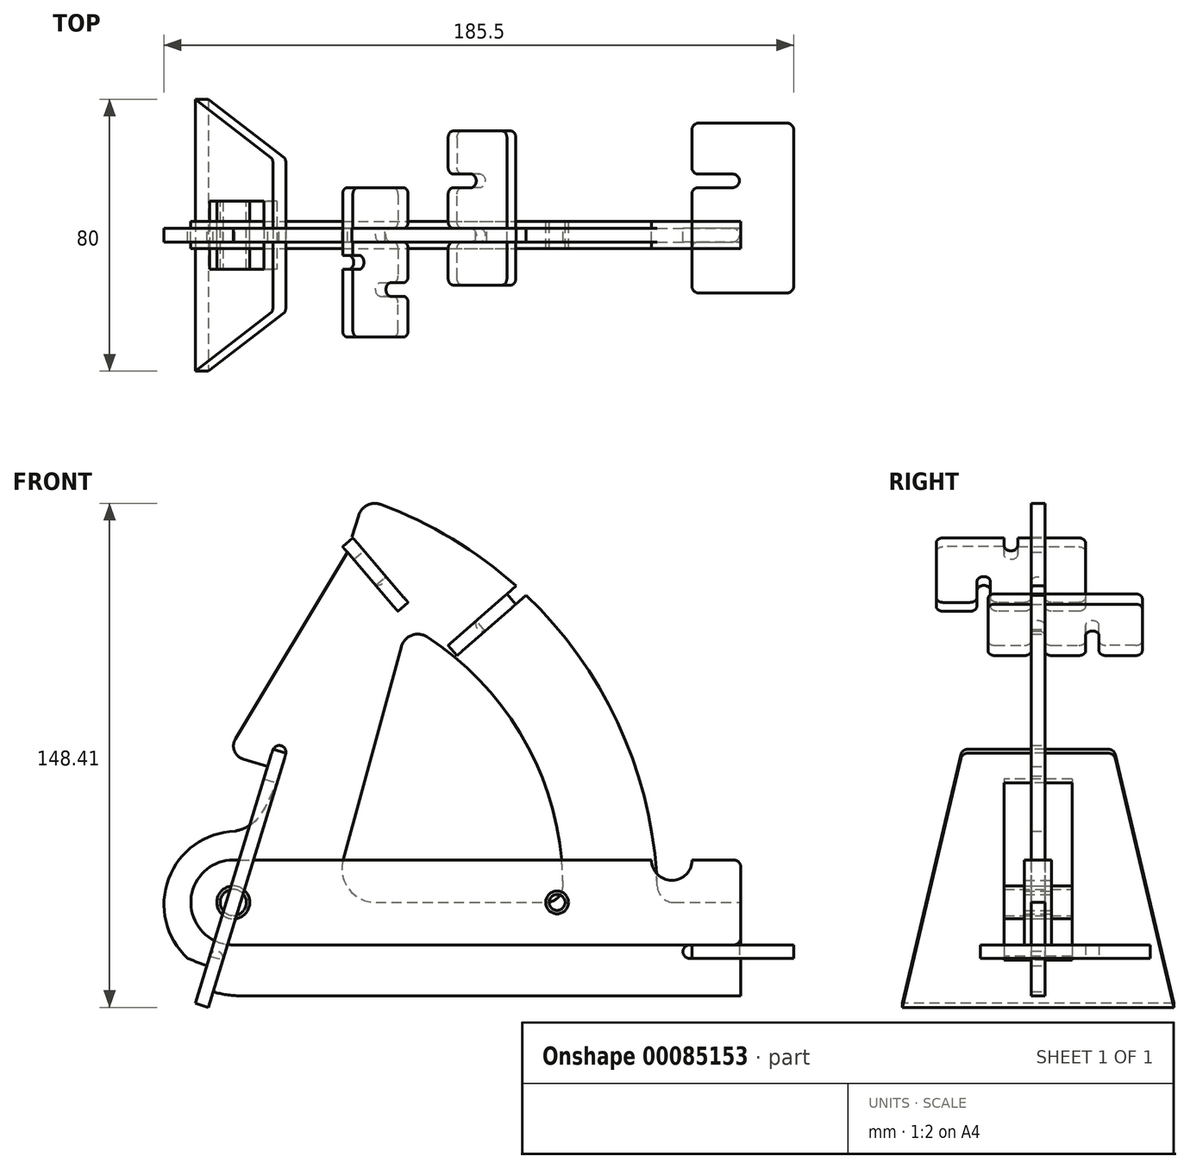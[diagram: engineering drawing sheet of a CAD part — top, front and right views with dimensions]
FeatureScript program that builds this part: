
annotation { "Feature Type Name" : "Feature", "Feature Type Description" : "" }
export const myFeature = defineFeature(function(context is Context, id is Id, definition is map)
    precondition{}
    {
        {
            var Q0;
            Q0=qCreatedBy(makeId("Front.planeOp"),FACE);
            var sketch = newSketch(context, id + "F0", { "sketchPlane" : qUnion([Q0])});
            skLineSegment(sketch, "E0", {"start": v(39.9, 0) * mm, "end": v(90.03, 0) * mm});
            skLineSegment(sketch, "E1.trimOffspring", {"start": v(31.52, 103.11) * mm, "end": v(34.85, 113.98) * mm});
            skLineSegment(sketch, "E2", {"start": v(0, -27.5) * mm, "end": v(147.4, -27.5) * mm});
            skPoint(sketch, "E3", {"position": v(95.8, 102.09) * mm});
            skArc(sketch, "E4", {"start": v(-27.2, -4.05) * mm, "mid": v(-27.13, -4.48) * mm, "end": v(-27.06, -4.91) * mm});
            skLineSegment(sketch, "E5", {"start": v(205.4, -14.5) * mm, "end": v(168.54, -14.5) * mm, "construction": true});
            skLineSegment(sketch, "E6", {"start": v(147.4, -14.5) * mm, "end": v(132.4, -14.5) * mm});
            skArc(sketch, "E7.0.endCap", {"start": v(132.4, -16.5) * mm, "mid": v(130.4, -14.5) * mm, "end": v(132.4, -12.5) * mm});
            skLineSegment(sketch, "E7.0.left", {"start": v(147.4, -16.5) * mm, "end": v(132.4, -16.5) * mm});
            skLineSegment(sketch, "E7.0.right", {"start": v(147.4, -12.5) * mm, "end": v(132.4, -12.5) * mm});
            skLineSegment(sketch, "E8", {"start": v(71.33, 81.91) * mm, "end": v(102.2, 108.89) * mm});
            skArc(sketch, "E9.0.startCap", {"start": v(72.62, 80.38) * mm, "mid": v(69.81, 80.6) * mm, "end": v(70.01, 83.42) * mm});
            skArc(sketch, "E9.0.endCap", {"start": v(100.87, 110.4) * mm, "mid": v(103.7, 110.2) * mm, "end": v(103.5, 107.38) * mm});
            skLineSegment(sketch, "E9.0.left", {"start": v(70.01, 83.42) * mm, "end": v(100.87, 110.4) * mm});
            skLineSegment(sketch, "E9.0.right", {"start": v(85.33, 91.49) * mm, "end": v(103.5, 107.38) * mm});
            skLineSegment(sketch, "E10", {"start": v(-8.04, -26.3) * mm, "end": v(-8.04, -26.3) * mm});
            skLineSegment(sketch, "E11", {"start": v(47.42, 75.33) * mm, "end": v(30.26, 12.64) * mm});
            skArc(sketch, "E12.filletArc", {"start": v(30.26, 12.64) * mm, "mid": v(31.95, 3.93) * mm, "end": v(39.9, 0) * mm});
            skPoint(sketch, "E13.visualSharp", {"position": v(52.17, 92.67) * mm});
            skPoint(sketch, "E14.endSnap0", {"position": v(-12.5, 0) * mm});
            skLineSegment(sketch, "E15", {"start": v(22.8, 74.55) * mm, "end": v(7.16, 23.42) * mm});
            skLineSegment(sketch, "E16", {"start": v(17.75, 71.72) * mm, "end": v(-20.77, -54.27) * mm, "construction": true});
            skPoint(sketch, "E17.startSnap0", {"position": v(11.4, 37.28) * mm});
            skLineSegment(sketch, "E18", {"start": v(4.72, 22.28) * mm, "end": v(-9.93, -25.64) * mm, "construction": true});
            skLineSegment(sketch, "E19", {"start": v(-7.1, -16.37) * mm, "end": v(-12.67, -34.6) * mm});
            skArc(sketch, "E20.0.startCap", {"start": v(-9, -15.78) * mm, "mid": v(-6.51, -14.46) * mm, "end": v(-5.18, -16.95) * mm});
            skLineSegment(sketch, "E20.0.left", {"start": v(-5.18, -16.95) * mm, "end": v(-10.77, -35.22) * mm});
            skLineSegment(sketch, "E20.0.right", {"start": v(-9, -15.78) * mm, "end": v(-14.6, -34.05) * mm});
            skPoint(sketch, "E21.visualSharp", {"position": v(-27.5, 0) * mm});
            skArc(sketch, "E22", {"start": v(95.03, 5.02) * mm, "mid": v(84.27, 46.7) * mm, "end": v(54.95, 78.21) * mm});
            skLineSegment(sketch, "E23", {"start": v(-60.53, 0) * mm, "end": v(147.4, 0) * mm, "construction": true});
            skCircle(sketch, "E24", {"center": v(-2.1, 0) * mm, "radius": 4.85 * mm});
            skArc(sketch, "E25", {"start": v(-2.1, 12.5) * mm, "mid": v(-14.6, 0) * mm, "end": v(-2.1, -12.5) * mm});
            skLineSegment(sketch, "E26", {"start": v(86.7, 92.43) * mm, "end": v(-27.06, -4.91) * mm, "construction": true});
            skLineSegment(sketch, "E27", {"start": v(147.4, 0) * mm, "end": v(147.4, -27.5) * mm});
            skPoint(sketch, "E28.visualSharp", {"position": v(124.1, 0) * mm});
            skPoint(sketch, "E29.visualSharp", {"position": v(49.15, 81.65) * mm});
            skArc(sketch, "E29.filletArc", {"start": v(54.95, 78.21) * mm, "mid": v(50.46, 78.68) * mm, "end": v(47.42, 75.33) * mm});
            skPoint(sketch, "E30.visualSharp", {"position": v(94.9, 0) * mm});
            skArc(sketch, "E30.filletArc", {"start": v(90.03, 0) * mm, "mid": v(93.57, 1.47) * mm, "end": v(95.03, 5.02) * mm});
            skLineSegment(sketch, "E31", {"start": v(32.22, 105.38) * mm, "end": v(61.64, 70.99) * mm, "construction": true});
            skLineSegment(sketch, "E32", {"start": v(32.22, 105.38) * mm, "end": v(24.37, 114.54) * mm, "construction": true});
            skLineSegment(sketch, "E33", {"start": v(40.67, 95.5) * mm, "end": v(30.35, 107.56) * mm});
            skArc(sketch, "E34.0.startCap", {"start": v(42.19, 96.8) * mm, "mid": v(41.97, 93.98) * mm, "end": v(39.15, 94.2) * mm});
            skArc(sketch, "E34.0.endCap", {"start": v(28.83, 106.26) * mm, "mid": v(29.05, 109.08) * mm, "end": v(31.87, 108.86) * mm});
            skLineSegment(sketch, "E34.0.left", {"start": v(39.15, 94.2) * mm, "end": v(28.83, 106.26) * mm});
            skLineSegment(sketch, "E34.0.right", {"start": v(42.19, 96.8) * mm, "end": v(31.87, 108.86) * mm});
            skPoint(sketch, "E35.orphan", {"position": v(49.12, 85.62) * mm});
            skArc(sketch, "E36", {"start": v(-9.88, -18.62) * mm, "mid": v(-12.73, -17.58) * mm, "end": v(-15.53, -16.42) * mm});
            skArc(sketch, "E37.trimOffspring", {"start": v(-8.04, -26.3) * mm, "mid": v(-4.06, -27.2) * mm, "end": v(0, -27.5) * mm});
            skLineSegment(sketch, "E38", {"start": v(-2.1, 12.5) * mm, "end": v(147.4, 12.5) * mm});
            skLineSegment(sketch, "E39", {"start": v(-2.1, -12.5) * mm, "end": v(147.4, -12.5) * mm});
            skArc(sketch, "E40", {"start": v(61.64, 70.99) * mm, "mid": v(85.04, 38.87) * mm, "end": v(93.31, 0) * mm, "construction": true});
            skCircle(sketch, "E41", {"center": v(93.31, 0) * mm, "radius": 3.35 * mm});
            skLineSegment(sketch, "E42", {"start": v(147.4, -12.5) * mm, "end": v(147.4, 12.5) * mm});
            skCircle(sketch, "E43", {"center": v(127.1, 12.5) * mm, "radius": 6 * mm});
            skArc(sketch, "E44", {"start": v(122.82, 4.8) * mm, "mid": v(99.13, 73.35) * mm, "end": v(41.37, 117.2) * mm});
            skLineSegment(sketch, "E45", {"start": v(122.9, 0) * mm, "end": v(122.9, -27.5) * mm, "construction": true});
            skPoint(sketch, "E46.visualSharp", {"position": v(36.36, 118.94) * mm});
            skArc(sketch, "E46.filletArc", {"start": v(41.37, 117.2) * mm, "mid": v(37.41, 117) * mm, "end": v(34.85, 113.98) * mm});
            skLineSegment(sketch, "E47", {"start": v(70.01, 83.42) * mm, "end": v(72.62, 80.38) * mm, "construction": true});
            skLineSegment(sketch, "E48", {"start": v(127.81, 0) * mm, "end": v(147.4, 0) * mm});
            skPoint(sketch, "E49.visualSharp", {"position": v(122.9, 0) * mm});
            skArc(sketch, "E49.filletArc", {"start": v(122.82, 4.8) * mm, "mid": v(124.35, 1.4) * mm, "end": v(127.81, 0) * mm});
            skLineSegment(sketch, "E50", {"start": v(72.62, 80.38) * mm, "end": v(85.33, 91.49) * mm});
            skLineSegment(sketch, "E51", {"start": v(11.43, 44.22) * mm, "end": v(9.97, 39.44) * mm});
            skArc(sketch, "E52.0.startCap", {"start": v(9.52, 44.8) * mm, "mid": v(12.01, 46.14) * mm, "end": v(13.34, 43.64) * mm});
            skLineSegment(sketch, "E52.0.left", {"start": v(13.34, 43.64) * mm, "end": v(11.88, 38.86) * mm});
            skLineSegment(sketch, "E52.0.right", {"start": v(9.52, 44.8) * mm, "end": v(8.05, 40.03) * mm});
            skLineSegment(sketch, "E53", {"start": v(0, -27.5) * mm, "end": v(-37.92, -27.5) * mm, "construction": true});
            skPoint(sketch, "E54", {"position": v(-10.5, -27.5) * mm});
            skLineSegment(sketch, "E55", {"start": v(8.05, 40.03) * mm, "end": v(0.8, 42.25) * mm});
            skPoint(sketch, "E56.visualSharp", {"position": v(-5.3, 44.1) * mm});
            skArc(sketch, "E56.filletArc", {"start": v(-1.47, 48.13) * mm, "mid": v(-1.77, 44.64) * mm, "end": v(0.8, 42.25) * mm});
            skLineSegment(sketch, "E57", {"start": v(-1.47, 48.13) * mm, "end": v(31.52, 103.11) * mm});
            skFitSpline(sketch, "E58", {"points": [v(11.4, 37.28) * mm, v(4.32, 23.93) * mm, v(-1.58, 20.95) * mm], "startDerivative": vector(-10.84, -26.6) * mm, "endDerivative": vector(-15.43, -4.6) * mm});
            skArc(sketch, "E59.trimOffspring", {"start": v(-1.58, 20.95) * mm, "mid": v(-21.15, 6.97) * mm, "end": v(-15.53, -16.42) * mm});
            skCircle(sketch, "E60", {"center": v(-2.1, 0) * mm, "radius": 3.85 * mm});
            skCircle(sketch, "E61", {"center": v(93.31, 0) * mm, "radius": 2.35 * mm});
            skSolve(sketch);
        }
        {
            var Q0;
            {var subQ0=sQuery(id+"F0.wireOp",EDGE,"bf617d19-ef6b-4165-97db-2c77cec7c9c5");var subQ1=sQuery(id+"F0.wireOp",EDGE,"E0");var subQ2=makeQuery(id+"F0.imprint","INTERSECT",VERTEX,{"disambiguationData":[OD(0.0)],"derivedFrom":[subQ1,subQ0]});Q0=makeQuery(id+"F0.imprint","IMPRINT",FACE,{"disambiguationData":[TD([[makeQuery(id+"F0.imprint","IMPRINT",EDGE,{"disambiguationData":[TD([[subQ2,-1.0]])],"derivedFrom":subQ1}),-1.0]])]});}
            var Q1;
            {var subQ13=sQuery(id+"F0.wireOp",EDGE,"634d09b6-26d1-4d0d-8a2f-190011938a09");Q1=makeQuery(id+"F0.imprint","IMPRINT",FACE,{"disambiguationData":[TD([[makeQuery(id+"F0.imprint","IMPRINT",EDGE,{"derivedFrom":subQ13}),-1.0]])]});}
            var Q2;
            {var subQ11=sQuery(id+"F0.wireOp",EDGE,"634d09b6-26d1-4d0d-8a2f-190011938a09");Q2=makeQuery(id+"F0.imprint","IMPRINT",FACE,{"disambiguationData":[TD([[makeQuery(id+"F0.imprint","IMPRINT",EDGE,{"derivedFrom":subQ11}),1.0]])]});}
            var Q3;
            {var subQ1=sQuery(id+"F0.wireOp",EDGE,"f24d4ff7-ed1b-4c84-8cf0-a38a7c947f8a.converted");var subQ3=sQuery(id+"F0.wireOp",EDGE,"88331fb1-bad4-4c96-8eaa-def0ac8052ee");var subQ4=makeQuery(id+"F0.imprint","INTERSECT",VERTEX,{"disambiguationData":[OD(0.0)],"derivedFrom":[subQ1,subQ3]});Q3=makeQuery(id+"F0.imprint","IMPRINT",FACE,{"disambiguationData":[TD([[makeQuery(id+"F0.imprint","IMPRINT",EDGE,{"disambiguationData":[TD([[subQ4,-1.0]])],"derivedFrom":subQ3}),1.0]])]});}
            var Q4;
            {var subQ1=sQuery(id+"F0.wireOp",EDGE,"f24d4ff7-ed1b-4c84-8cf0-a38a7c947f8a.converted");var subQ3=sQuery(id+"F0.wireOp",EDGE,"88331fb1-bad4-4c96-8eaa-def0ac8052ee");var subQ4=makeQuery(id+"F0.imprint","INTERSECT",VERTEX,{"disambiguationData":[OD(1.0)],"derivedFrom":[subQ1,subQ3]});Q4=makeQuery(id+"F0.imprint","IMPRINT",FACE,{"disambiguationData":[TD([[makeQuery(id+"F0.imprint","IMPRINT",EDGE,{"disambiguationData":[TD([[subQ4,1.0]])],"derivedFrom":subQ3}),1.0]])]});}
            var Q5;
            {var subQ9=sQuery(id+"F0.wireOp",EDGE,"1a92d0de-3d02-4553-99da-0eeac4e26b29.filletArc");Q5=makeQuery(id+"F0.imprint","IMPRINT",FACE,{"disambiguationData":[TD([[makeQuery(id+"F0.imprint","IMPRINT",EDGE,{"derivedFrom":subQ9}),1.0]])]});}
            var Q6;
            {var subQ7=sQuery(id+"F0.wireOp",EDGE,"E2");Q6=makeQuery(id+"F0.imprint","IMPRINT",FACE,{"disambiguationData":[TD([[makeQuery(id+"F0.imprint","IMPRINT",EDGE,{"derivedFrom":subQ7}),1.0]])]});}
            var Q7;
            {var subQ2=sQuery(id+"F0.wireOp",EDGE,"NjWoISIm-s9i9-YRtm-21tn-n0SVHgzNwCzY");Q7=makeQuery(id+"F0.imprint","IMPRINT",FACE,{"disambiguationData":[TD([[makeQuery(id+"F0.imprint","IMPRINT",EDGE,{"derivedFrom":subQ2}),-1.0]])]});}
            var Q8;
            {var subQ0=sQuery(id+"F0.wireOp",EDGE,"E28.filletArc");var subQ1=sQuery(id+"F0.wireOp",EDGE,"f24d4ff7-ed1b-4c84-8cf0-a38a7c947f8a.converted");var subQ2=makeQuery(id+"F0.imprint","INTERSECT",VERTEX,{"derivedFrom":[subQ1,subQ0]});Q8=makeQuery(id+"F0.imprint","IMPRINT",FACE,{"disambiguationData":[TD([[makeQuery(id+"F0.imprint","IMPRINT",EDGE,{"disambiguationData":[TD([[subQ2,-1.0]])],"derivedFrom":subQ1}),1.0]])]});}
            var Q9;
            {var subQ0=sQuery(id+"F0.wireOp",EDGE,"E43");var subQ1=sQuery(id+"F0.wireOp",EDGE,"f24d4ff7-ed1b-4c84-8cf0-a38a7c947f8a.converted");var subQ2=makeQuery(id+"F0.imprint","INTERSECT",VERTEX,{"derivedFrom":[subQ1,subQ0]});Q9=makeQuery(id+"F0.imprint","IMPRINT",FACE,{"disambiguationData":[TD([[makeQuery(id+"F0.imprint","IMPRINT",EDGE,{"disambiguationData":[TD([[subQ2,1.0]])],"derivedFrom":subQ1}),1.0]])]});}
            var Q10;
            Q10=makeQuery(id+"F0.imprint","IMPRINT",FACE,{"disambiguationData":[TD([[makeQuery(id+"F0.imprint","IMPRINT",EDGE,{"derivedFrom":sQuery(id+"F0.wireOp",EDGE,"E24")}),-1.0]])]});
            var Q11;
            {var subQ19=sQuery(id+"F0.wireOp",EDGE,"E11");Q11=makeQuery(id+"F0.imprint","IMPRINT",FACE,{"disambiguationData":[TD([[makeQuery(id+"F0.imprint","IMPRINT",EDGE,{"derivedFrom":subQ19}),-1.0]])]});}
            var Q12;
            {var subQ0=sQuery(id+"F0.wireOp",EDGE,"E43");var subQ1=sQuery(id+"F0.wireOp",EDGE,"E38");var subQ2=makeQuery(id+"F0.imprint","INTERSECT",VERTEX,{"disambiguationData":[OD(1.0)],"derivedFrom":[subQ1,subQ0]});Q12=makeQuery(id+"F0.imprint","IMPRINT",FACE,{"disambiguationData":[TD([[makeQuery(id+"F0.imprint","IMPRINT",EDGE,{"disambiguationData":[TD([[subQ2,-1.0]])],"derivedFrom":subQ1}),1.0]])]});}
            var Q13;
            {var subQ0=sQuery(id+"F0.wireOp",EDGE,"E43");var subQ1=sQuery(id+"F0.wireOp",EDGE,"E38");var subQ2=makeQuery(id+"F0.imprint","INTERSECT",VERTEX,{"disambiguationData":[OD(1.0)],"derivedFrom":[subQ1,subQ0]});Q13=makeQuery(id+"F0.imprint","IMPRINT",FACE,{"disambiguationData":[TD([[makeQuery(id+"F0.imprint","IMPRINT",EDGE,{"disambiguationData":[TD([[subQ2,-1.0]])],"derivedFrom":subQ1}),-1.0]])]});}
            var Q14;
            {var subQ0=sQuery(id+"F0.wireOp",EDGE,"E61");var subQ1=sQuery(id+"F0.wireOp",EDGE,"E30.filletArc");var subQ2=makeQuery(id+"F0.imprint","INTERSECT",VERTEX,{"disambiguationData":[OD(0.0)],"derivedFrom":[subQ1,subQ0]});Q14=makeQuery(id+"F0.imprint","IMPRINT",FACE,{"disambiguationData":[TD([[makeQuery(id+"F0.imprint","IMPRINT",EDGE,{"disambiguationData":[TD([[subQ2,-1.0]])],"derivedFrom":subQ1}),-1.0]])]});}
            extrude(context, id + "F1", {"entities" : qUnion([Q0, Q1, Q2, Q3, Q4, Q5, Q6, Q7, Q8, Q9, Q10, Q11, Q12, Q13, Q14]), "endBound" : BoundingType.SYMMETRIC, "depth" : 4 * mm});
        }
        {
            var Q0;
            Q0=makeQuery(id+"F1.opExtrude","SWEPT_FACE",FACE,{"disambiguationData":[OSD([sQuery(id+"F0.wireOp",EDGE,"E20.0.left")])]});
            cPlane(context, id + "F2", {"entities" : qUnion([Q0]), "cplaneType" : CPlaneType.OFFSET, "offset" : 2 * mm, "width" : 150 * mm, "height" : 150 * mm});
        }
        {
            var Q0;
            Q0=qCreatedBy(id+"F2.planeOp",FACE);
            var sketch = newSketch(context, id + "F3", { "sketchPlane" : qUnion([Q0])});
            skLineSegment(sketch, "E62", {"start": v(-10, 36.82) * mm, "end": v(-10, -17.73) * mm});
            skLineSegment(sketch, "E63", {"start": v(-10, -17.73) * mm, "end": v(0, -17.73) * mm});
            skLineSegment(sketch, "E64", {"start": v(0, 0) * mm, "end": v(0, 60.64) * mm, "construction": true});
            skPoint(sketch, "E65.orphan", {"position": v(-2, -17.73) * mm});
            skLineSegment(sketch, "E66", {"start": v(0, 60.64) * mm, "end": v(0, -32.3) * mm, "construction": true});
            skLineSegment(sketch, "E67", {"start": v(-40, -32.3) * mm, "end": v(0, -32.3) * mm});
            skLineSegment(sketch, "E68.MirrorCS", {"start": v(10, -17.73) * mm, "end": v(0, -17.73) * mm});
            skLineSegment(sketch, "E69.MirrorCS", {"start": v(40, -32.3) * mm, "end": v(0, -32.3) * mm});
            skPoint(sketch, "E70.MirrorP", {"position": v(2, -17.73) * mm});
            skLineSegment(sketch, "E71.MirrorCS", {"start": v(10, 56.95) * mm, "end": v(10, -17.73) * mm, "construction": true});
            skLineSegment(sketch, "E72.MirrorCS", {"start": v(10, 36.82) * mm, "end": v(10, -17.73) * mm});
            skLineSegment(sketch, "E73", {"start": v(40, -32.3) * mm, "end": v(22.37, 45.94) * mm});
            skPoint(sketch, "E74.start.orphan", {"position": v(0, 66.93) * mm});
            skLineSegment(sketch, "E75.MirrorCS", {"start": v(-40, -32.3) * mm, "end": v(-22.37, 45.94) * mm});
            skLineSegment(sketch, "E76.0.3", {"start": v(2, -17.73) * mm, "end": v(-2, -17.73) * mm});
            skLineSegment(sketch, "E77.0.1", {"start": v(-2, -17.73) * mm, "end": v(2, -17.73) * mm});
            skLineSegment(sketch, "E78", {"start": v(-10, 36.82) * mm, "end": v(10, 36.82) * mm});
            skLineSegment(sketch, "E79", {"start": v(-22.37, 45.94) * mm, "end": v(22.37, 45.94) * mm});
            skPoint(sketch, "E80.end.orphan", {"position": v(0, 56.95) * mm});
            skPoint(sketch, "E81.orphan", {"position": v(2, -27.5) * mm});
            skPoint(sketch, "E76.0.1.start.orphan", {"position": v(-2, -27.5) * mm});
            skPoint(sketch, "E76.0.0.end.orphan", {"position": v(-2, -20.7) * mm});
            skPoint(sketch, "E77.0.2.end.orphan", {"position": v(2, -20.7) * mm});
            skSolve(sketch);
        }
        {
            var Q0;
            Q0=qSketchRegion(id+"F3",true);
            extrude(context, id + "F4", {"entities" : qUnion([Q0]), "endBound" : BoundingType.SYMMETRIC, "depth" : 4 * mm});
        }
        {
            var Q0;
            Q0=makeQuery(id+"F0.imprint","IMPRINT",FACE,{"disambiguationData":[TD([[makeQuery(id+"F0.imprint","IMPRINT",EDGE,{"derivedFrom":sQuery(id+"F0.wireOp",EDGE,"E24")}),-1.0]])]});
            var Q1;
            {var subQ7=sQuery(id+"F0.wireOp",EDGE,"E12.filletArc");var subQ8=sQuery(id+"F0.wireOp",EDGE,"E0");var subQ9=makeQuery(id+"F0.imprint","INTERSECT",VERTEX,{"derivedFrom":[subQ8,subQ7]});Q1=makeQuery(id+"F0.imprint","IMPRINT",FACE,{"disambiguationData":[TD([[makeQuery(id+"F0.imprint","IMPRINT",EDGE,{"disambiguationData":[TD([[subQ9,-1.0]])],"derivedFrom":subQ8}),1.0]])]});}
            var Q2;
            {var subQ8=sQuery(id+"F0.wireOp",EDGE,"E48");Q2=makeQuery(id+"F0.imprint","IMPRINT",FACE,{"disambiguationData":[TD([[makeQuery(id+"F0.imprint","IMPRINT",EDGE,{"derivedFrom":subQ8}),1.0]])]});}
            extrude(context, id + "F5", {"entities" : qUnion([Q0, Q1, Q2]), "endBound" : BoundingType.SYMMETRIC, "depth" : 8 * mm});
        }
        {
            var Q0;
            Q0=makeQuery(id+"F1.opExtrude","SWEPT_FACE",FACE,{"disambiguationData":[OSD([sQuery(id+"F0.wireOp",EDGE,"E34.0.right")])]});
            cPlane(context, id + "F6", {"entities" : qUnion([Q0]), "cplaneType" : CPlaneType.OFFSET, "offset" : 2 * mm, "width" : 150 * mm, "height" : 150 * mm});
        }
        {
            var Q0;
            Q0=qCreatedBy(id+"F6.planeOp",FACE);
            var sketch = newSketch(context, id + "F7", { "sketchPlane" : qUnion([Q0])});
            skLineSegment(sketch, "E82", {"start": v(8, 72.78) * mm, "end": v(8, 41.54) * mm, "construction": true});
            skLineSegment(sketch, "E83", {"start": v(8, 60.02) * mm, "end": v(-14, 60.02) * mm});
            skLineSegment(sketch, "E84", {"start": v(-14, 60.02) * mm, "end": v(-14, 35.02) * mm});
            skLineSegment(sketch, "E85", {"start": v(-14, 35.02) * mm, "end": v(-2, 35.02) * mm});
            skLineSegment(sketch, "E86", {"start": v(-2, 35.02) * mm, "end": v(-2, 43.02) * mm});
            skLineSegment(sketch, "E87", {"start": v(2, 43.02) * mm, "end": v(2, 35.02) * mm});
            skLineSegment(sketch, "E88", {"start": v(2, 35.02) * mm, "end": v(8, 35.02) * mm});
            skLineSegment(sketch, "E89.MirrorCS", {"start": v(8, 60.02) * mm, "end": v(30, 60.02) * mm});
            skLineSegment(sketch, "E90.MirrorCS", {"start": v(30, 60.02) * mm, "end": v(30, 35.02) * mm});
            skLineSegment(sketch, "E91.MirrorCS", {"start": v(30, 35.02) * mm, "end": v(18, 35.02) * mm});
            skLineSegment(sketch, "E92.MirrorCS", {"start": v(18, 35.02) * mm, "end": v(18, 43.02) * mm});
            skLineSegment(sketch, "E93.MirrorCS", {"start": v(14, 43.02) * mm, "end": v(14, 35.02) * mm});
            skLineSegment(sketch, "E94.MirrorCS", {"start": v(14, 35.02) * mm, "end": v(8, 35.02) * mm});
            skArc(sketch, "E95", {"start": v(2, 43.02) * mm, "mid": v(0, 45.02) * mm, "end": v(-2, 43.02) * mm});
            skArc(sketch, "E96.MirrorCS", {"start": v(14, 43.02) * mm, "mid": v(16, 45.02) * mm, "end": v(18, 43.02) * mm});
            skPoint(sketch, "E97.orphan", {"position": v(18, 43.02) * mm});
            skLineSegment(sketch, "E98", {"start": v(8, 62.87) * mm, "end": v(8, 57.02) * mm});
            skArc(sketch, "E99.0.startCap", {"start": v(6, 62.87) * mm, "mid": v(8, 64.87) * mm, "end": v(10, 62.87) * mm});
            skArc(sketch, "E99.0.endCap", {"start": v(10, 57.02) * mm, "mid": v(8, 55.02) * mm, "end": v(6, 57.02) * mm});
            skLineSegment(sketch, "E99.0.left", {"start": v(10, 62.87) * mm, "end": v(10, 57.02) * mm});
            skLineSegment(sketch, "E99.0.right", {"start": v(6, 62.87) * mm, "end": v(6, 57.02) * mm});
            skSolve(sketch);
        }
        {
            var Q0;
            {var subQ4=sQuery(id+"F7.wireOp",EDGE,"E84");Q0=makeQuery(id+"F7.imprint","IMPRINT",FACE,{"disambiguationData":[TD([[makeQuery(id+"F7.imprint","IMPRINT",EDGE,{"derivedFrom":subQ4}),1.0]])]});}
            extrude(context, id + "F8", {"entities" : qUnion([Q0]), "endBound" : BoundingType.SYMMETRIC, "depth" : 4 * mm});
        }
        {
            var Q0;
            Q0=makeQuery(id+"F1.opExtrude","SWEPT_FACE",FACE,{"disambiguationData":[OSD([sQuery(id+"F0.wireOp",EDGE,"E9.0.left")])]});
            cPlane(context, id + "F9", {"entities" : qUnion([Q0]), "cplaneType" : CPlaneType.OFFSET, "offset" : 2 * mm, "width" : 150 * mm, "height" : 150 * mm});
        }
        {
            var Q0;
            Q0=qCreatedBy(id+"F9.planeOp",FACE);
            var sketch = newSketch(context, id + "F10", { "sketchPlane" : qUnion([Q0])});
            skLineSegment(sketch, "E100.0.1", {"start": v(118.92, 2) * mm, "end": v(118.92, -2) * mm});
            skLineSegment(sketch, "E101", {"start": v(145.27, -8) * mm, "end": v(95.92, -8) * mm, "construction": true});
            skLineSegment(sketch, "E102", {"start": v(118.92, -8) * mm, "end": v(118.92, 14.7) * mm});
            skLineSegment(sketch, "E103", {"start": v(118.92, 14.7) * mm, "end": v(95.92, 14.7) * mm});
            skLineSegment(sketch, "E104", {"start": v(95.92, 14.7) * mm, "end": v(95.92, 2) * mm});
            skLineSegment(sketch, "E105", {"start": v(95.92, 2) * mm, "end": v(104.92, 2) * mm});
            skLineSegment(sketch, "E106", {"start": v(104.92, -2) * mm, "end": v(95.92, -2) * mm});
            skLineSegment(sketch, "E107", {"start": v(95.92, -2) * mm, "end": v(95.92, -8) * mm});
            skArc(sketch, "E108", {"start": v(104.92, -2) * mm, "mid": v(106.92, 0) * mm, "end": v(104.92, 2) * mm});
            skLineSegment(sketch, "E109.MirrorCS", {"start": v(118.92, -14) * mm, "end": v(118.92, -18) * mm});
            skLineSegment(sketch, "E110.MirrorCS", {"start": v(118.92, -30.7) * mm, "end": v(95.92, -30.7) * mm});
            skArc(sketch, "E111.MirrorCS", {"start": v(104.92, -14) * mm, "mid": v(106.92, -16) * mm, "end": v(104.92, -18) * mm});
            skLineSegment(sketch, "E112.MirrorCS", {"start": v(118.92, -8) * mm, "end": v(118.92, -30.7) * mm});
            skLineSegment(sketch, "E113.MirrorCS", {"start": v(95.92, -14) * mm, "end": v(95.92, -8) * mm});
            skLineSegment(sketch, "E114.MirrorCS", {"start": v(104.92, -14) * mm, "end": v(95.92, -14) * mm});
            skLineSegment(sketch, "E115.MirrorCS", {"start": v(95.92, -18) * mm, "end": v(104.92, -18) * mm});
            skLineSegment(sketch, "E116.MirrorCS", {"start": v(95.92, -30.7) * mm, "end": v(95.92, -18) * mm});
            skSolve(sketch);
        }
        {
            var Q0;
            Q0=qSketchRegion(id+"F10",true);
            extrude(context, id + "F11", {"entities" : qUnion([Q0]), "endBound" : BoundingType.SYMMETRIC, "depth" : 4 * mm});
        }
        {
            var Q0;
            Q0=makeQuery(id+"F1.opExtrude","SWEPT_FACE",FACE,{"disambiguationData":[OSD([sQuery(id+"F0.wireOp",EDGE,"E7.0.left")])]});
            cPlane(context, id + "F12", {"entities" : qUnion([Q0]), "cplaneType" : CPlaneType.OFFSET, "offset" : 2 * mm, "width" : 150 * mm, "height" : 150 * mm});
        }
        {
            var Q0;
            Q0=qCreatedBy(id+"F12.planeOp",FACE);
            var sketch = newSketch(context, id + "F13", { "sketchPlane" : qUnion([Q0])});
            skLineSegment(sketch, "E117", {"start": v(163, 8) * mm, "end": v(163, -17) * mm});
            skLineSegment(sketch, "E118", {"start": v(163, -17) * mm, "end": v(133, -17) * mm});
            skLineSegment(sketch, "E119", {"start": v(133, -17) * mm, "end": v(133, -2) * mm});
            skLineSegment(sketch, "E120", {"start": v(133, -2) * mm, "end": v(145, -2) * mm});
            skLineSegment(sketch, "E121", {"start": v(145, 2) * mm, "end": v(133, 2) * mm});
            skLineSegment(sketch, "E122", {"start": v(133, 2) * mm, "end": v(133, 8) * mm});
            skLineSegment(sketch, "E123", {"start": v(174.87, 8) * mm, "end": v(133, 8) * mm, "construction": true});
            skLineSegment(sketch, "E124.MirrorCS", {"start": v(133, 33) * mm, "end": v(133, 18) * mm});
            skLineSegment(sketch, "E125.MirrorCS", {"start": v(133, 18) * mm, "end": v(145, 18) * mm});
            skLineSegment(sketch, "E126.MirrorCS", {"start": v(133, 14) * mm, "end": v(133, 8) * mm});
            skLineSegment(sketch, "E127.MirrorCS", {"start": v(145, 14) * mm, "end": v(133, 14) * mm});
            skLineSegment(sketch, "E128.MirrorCS", {"start": v(163, 8) * mm, "end": v(163, 33) * mm});
            skLineSegment(sketch, "E129.MirrorCS", {"start": v(163, 33) * mm, "end": v(133, 33) * mm});
            skArc(sketch, "E130", {"start": v(145, -2) * mm, "mid": v(147, 0) * mm, "end": v(145, 2) * mm});
            skArc(sketch, "E131", {"start": v(145, 14) * mm, "mid": v(147, 16) * mm, "end": v(145, 18) * mm});
            skSolve(sketch);
        }
        {
            var Q0;
            Q0=qSketchRegion(id+"F13",true);
            extrude(context, id + "F14", {"entities" : qUnion([Q0]), "endBound" : BoundingType.SYMMETRIC, "depth" : 4 * mm});
        }
        {
            var Q0;
            Q0=makeQuery(id+"F11.opExtrude","SWEPT_EDGE",EDGE,{"disambiguationData":[OSD([sQuery(id+"F10.wireOp",EDGE,"E110.MirrorCS"),sQuery(id+"F10.wireOp",EDGE,"E116.MirrorCS")])]});
            var Q1;
            Q1=makeQuery(id+"F11.opExtrude","SWEPT_EDGE",EDGE,{"disambiguationData":[OSD([sQuery(id+"F10.wireOp",EDGE,"E115.MirrorCS"),sQuery(id+"F10.wireOp",EDGE,"E116.MirrorCS")])]});
            var Q2;
            Q2=makeQuery(id+"F11.opExtrude","SWEPT_EDGE",EDGE,{"disambiguationData":[OSD([sQuery(id+"F10.wireOp",EDGE,"E113.MirrorCS"),sQuery(id+"F10.wireOp",EDGE,"E114.MirrorCS")])]});
            var Q3;
            Q3=makeQuery(id+"F8.opExtrude","SWEPT_EDGE",EDGE,{"disambiguationData":[OSD([sQuery(id+"F7.wireOp",EDGE,"E84"),sQuery(id+"F7.wireOp",EDGE,"E85")])]});
            var Q4;
            Q4=makeQuery(id+"F8.opExtrude","SWEPT_EDGE",EDGE,{"disambiguationData":[OSD([sQuery(id+"F7.wireOp",EDGE,"E83"),sQuery(id+"F7.wireOp",EDGE,"E84")])]});
            var Q5;
            Q5=makeQuery(id+"F8.opExtrude","SWEPT_EDGE",EDGE,{"disambiguationData":[OSD([sQuery(id+"F7.wireOp",EDGE,"E91.MirrorCS"),sQuery(id+"F7.wireOp",EDGE,"E92.MirrorCS")])]});
            var Q6;
            Q6=makeQuery(id+"F11.opExtrude","SWEPT_EDGE",EDGE,{"disambiguationData":[OSD([sQuery(id+"F10.wireOp",EDGE,"E110.MirrorCS"),sQuery(id+"F10.wireOp",EDGE,"E112.MirrorCS")])]});
            var Q7;
            Q7=makeQuery(id+"F4.opExtrude","SWEPT_EDGE",EDGE,{"disambiguationData":[OSD([sQuery(id+"F3.wireOp",EDGE,"E75.MirrorCS"),sQuery(id+"F3.wireOp",EDGE,"E79")])]});
            var Q8;
            Q8=makeQuery(id+"F4.opExtrude","SWEPT_EDGE",EDGE,{"disambiguationData":[OSD([sQuery(id+"F3.wireOp",EDGE,"E73"),sQuery(id+"F3.wireOp",EDGE,"E79")])]});
            var Q9;
            Q9=makeQuery(id+"F11.opExtrude","SWEPT_EDGE",EDGE,{"disambiguationData":[OSD([sQuery(id+"F10.wireOp",EDGE,"E102"),sQuery(id+"F10.wireOp",EDGE,"E103")])]});
            var Q10;
            Q10=makeQuery(id+"F11.opExtrude","SWEPT_EDGE",EDGE,{"disambiguationData":[OSD([sQuery(id+"F10.wireOp",EDGE,"E103"),sQuery(id+"F10.wireOp",EDGE,"E104")])]});
            var Q11;
            Q11=makeQuery(id+"F8.opExtrude","SWEPT_EDGE",EDGE,{"disambiguationData":[OSD([sQuery(id+"F7.wireOp",EDGE,"E90.MirrorCS"),sQuery(id+"F7.wireOp",EDGE,"E91.MirrorCS")])]});
            var Q12;
            Q12=makeQuery(id+"F8.opExtrude","SWEPT_EDGE",EDGE,{"disambiguationData":[OSD([sQuery(id+"F7.wireOp",EDGE,"E93.MirrorCS"),sQuery(id+"F7.wireOp",EDGE,"E94.MirrorCS")])]});
            var Q13;
            Q13=makeQuery(id+"F8.opExtrude","SWEPT_EDGE",EDGE,{"disambiguationData":[OSD([sQuery(id+"F7.wireOp",EDGE,"E89.MirrorCS"),sQuery(id+"F7.wireOp",EDGE,"E90.MirrorCS")])]});
            var Q14;
            Q14=makeQuery(id+"F14.opExtrude","SWEPT_EDGE",EDGE,{"disambiguationData":[OSD([sQuery(id+"F13.wireOp",EDGE,"E117"),sQuery(id+"F13.wireOp",EDGE,"E118")])]});
            var Q15;
            Q15=makeQuery(id+"F14.opExtrude","SWEPT_EDGE",EDGE,{"disambiguationData":[OSD([sQuery(id+"F13.wireOp",EDGE,"E118"),sQuery(id+"F13.wireOp",EDGE,"E119")])]});
            var Q16;
            Q16=makeQuery(id+"F14.opExtrude","SWEPT_EDGE",EDGE,{"disambiguationData":[OSD([sQuery(id+"F13.wireOp",EDGE,"E128.MirrorCS"),sQuery(id+"F13.wireOp",EDGE,"E129.MirrorCS")])]});
            var Q17;
            Q17=makeQuery(id+"F14.opExtrude","SWEPT_EDGE",EDGE,{"disambiguationData":[OSD([sQuery(id+"F13.wireOp",EDGE,"E126.MirrorCS"),sQuery(id+"F13.wireOp",EDGE,"E127.MirrorCS")])]});
            var Q18;
            Q18=makeQuery(id+"F14.opExtrude","SWEPT_EDGE",EDGE,{"disambiguationData":[OSD([sQuery(id+"F13.wireOp",EDGE,"E124.MirrorCS"),sQuery(id+"F13.wireOp",EDGE,"E125.MirrorCS")])]});
            var Q19;
            Q19=makeQuery(id+"F14.opExtrude","SWEPT_EDGE",EDGE,{"disambiguationData":[OSD([sQuery(id+"F13.wireOp",EDGE,"E124.MirrorCS"),sQuery(id+"F13.wireOp",EDGE,"E129.MirrorCS")])]});
            var Q20;
            Q20=makeQuery(id+"F14.opExtrude","SWEPT_EDGE",EDGE,{"disambiguationData":[OSD([sQuery(id+"F13.wireOp",EDGE,"E119"),sQuery(id+"F13.wireOp",EDGE,"E120")])]});
            var Q21;
            Q21=makeQuery(id+"F11.opExtrude","SWEPT_EDGE",EDGE,{"disambiguationData":[OSD([sQuery(id+"F10.wireOp",EDGE,"E104"),sQuery(id+"F10.wireOp",EDGE,"E105")])]});
            var Q22;
            Q22=makeQuery(id+"F11.opExtrude","SWEPT_EDGE",EDGE,{"disambiguationData":[OSD([sQuery(id+"F10.wireOp",EDGE,"E106"),sQuery(id+"F10.wireOp",EDGE,"E107")])]});
            var Q23;
            Q23=makeQuery(id+"F8.opExtrude","SWEPT_EDGE",EDGE,{"disambiguationData":[OSD([sQuery(id+"F7.wireOp",EDGE,"E85"),sQuery(id+"F7.wireOp",EDGE,"E86")])]});
            var Q24;
            Q24=makeQuery(id+"F8.opExtrude","SWEPT_EDGE",EDGE,{"disambiguationData":[OSD([sQuery(id+"F7.wireOp",EDGE,"E87"),sQuery(id+"F7.wireOp",EDGE,"E88")])]});
            var Q25;
            Q25=makeQuery(id+"F5.opExtrude","SWEPT_EDGE",EDGE,{"disambiguationData":[OSD([sQuery(id+"F0.wireOp",EDGE,"E38"),sQuery(id+"F0.wireOp",EDGE,"E42")])]});
            var Q26;
            Q26=makeQuery(id+"F5.opExtrude","SWEPT_EDGE",EDGE,{"disambiguationData":[OSD([sQuery(id+"F0.wireOp",EDGE,"E27"),sQuery(id+"F0.wireOp",EDGE,"E39"),sQuery(id+"F0.wireOp",EDGE,"E42")])]});
            fillet(context, id + "F15", {"entities" : qUnion([Q0, Q1, Q2, Q3, Q4, Q5, Q6, Q7, Q8, Q9, Q10, Q11, Q12, Q13, Q14, Q15, Q16, Q17, Q18, Q19, Q20, Q21, Q22, Q23, Q24, Q25, Q26]), "radius" : 2 * mm, "tangentPropagation" : true, "allowEdgeOverflow" : false});
        }
        {
            var Q0;
            Q0=makeQuery(id+"F0.imprint","IMPRINT",FACE,{"disambiguationData":[TD([[makeQuery(id+"F0.imprint","IMPRINT",EDGE,{"derivedFrom":sQuery(id+"F0.wireOp",EDGE,"E24")}),1.0]])]});
            extrude(context, id + "F16", {"entities" : qUnion([Q0]), "endBound" : BoundingType.SYMMETRIC, "depth" : 20 * mm});
        }
        {
            var Q0;
            {var subQ1=sQuery(id+"F0.wireOp",EDGE,"E30.filletArc");var subQ5=sQuery(id+"F0.wireOp",EDGE,"E0");var subQ6=makeQuery(id+"F0.imprint","INTERSECT",VERTEX,{"derivedFrom":[subQ5,subQ1]});Q0=makeQuery(id+"F0.imprint","IMPRINT",FACE,{"disambiguationData":[TD([[makeQuery(id+"F0.imprint","IMPRINT",EDGE,{"disambiguationData":[TD([[subQ6,1.0]])],"derivedFrom":subQ5}),1.0]])]});}
            var Q1;
            {var subQ1=sQuery(id+"F0.wireOp",EDGE,"E0");var subQ3=sQuery(id+"F0.wireOp",EDGE,"E30.filletArc");var subQ7=makeQuery(id+"F0.imprint","INTERSECT",VERTEX,{"derivedFrom":[subQ1,subQ3]});Q1=makeQuery(id+"F0.imprint","IMPRINT",FACE,{"disambiguationData":[TD([[makeQuery(id+"F0.imprint","IMPRINT",EDGE,{"disambiguationData":[TD([[subQ7,1.0]])],"derivedFrom":subQ1}),-1.0]])]});}
            extrude(context, id + "F17", {"entities" : qUnion([Q0, Q1]), "endBound" : BoundingType.SYMMETRIC, "depth" : 8 * mm});
        }
    });
